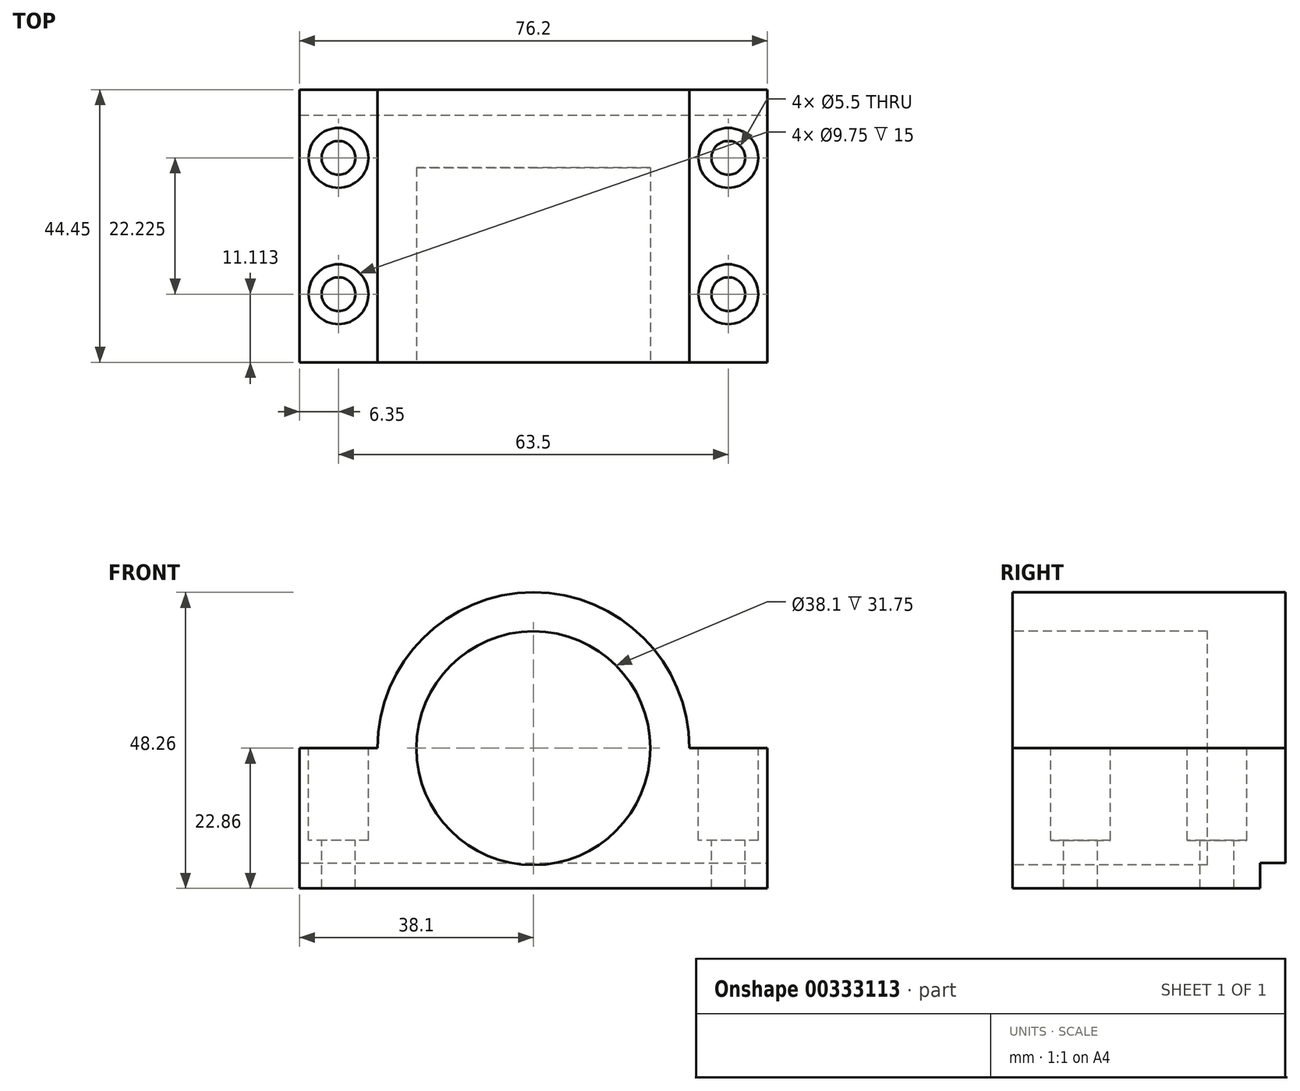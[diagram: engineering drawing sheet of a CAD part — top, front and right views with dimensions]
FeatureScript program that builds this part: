
annotation { "Feature Type Name" : "Feature", "Feature Type Description" : "" }
export const myFeature = defineFeature(function(context is Context, id is Id, definition is map)
    precondition{}
    {
        {
            var Q0;
            Q0=qCreatedBy(makeId("Front.planeOp"),FACE);
            var sketch = newSketch(context, id + "F0", { "sketchPlane" : qUnion([Q0])});
            skLineSegment(sketch, "E0.bottom", {"start": v(-38.1, -25.4) * mm, "end": v(38.1, -25.4) * mm});
            skLineSegment(sketch, "E0.top", {"start": v(-38.1, 25.4) * mm, "end": v(38.1, 25.4) * mm});
            skLineSegment(sketch, "E0.left", {"start": v(-38.1, -25.4) * mm, "end": v(-38.1, 25.4) * mm});
            skLineSegment(sketch, "E0.right", {"start": v(38.1, -25.4) * mm, "end": v(38.1, 25.4) * mm});
            skPoint(sketch, "E0.middle", {"position": v(0, 0) * mm});
            skSolve(sketch);
        }
        {
            var Q0;
            Q0=qSketchRegion(id+"F0",true);
            extrude(context, id + "F1", {"entities" : qUnion([Q0]), "depth" : 44.45 * mm});
        }
        {
            var Q0;
            Q0=makeQuery(id+"F1.opExtrude","CAP_FACE",FACE,{"disambiguationData":[OSD([sQuery(id+"F0.wireOp",EDGE,"E0.bottom"),sQuery(id+"F0.wireOp",EDGE,"E0.top"),sQuery(id+"F0.wireOp",EDGE,"E0.left"),sQuery(id+"F0.wireOp",EDGE,"E0.right")])],"isStart":false});
            var sketch = newSketch(context, id + "F2", { "sketchPlane" : qUnion([Q0])});
            skCircle(sketch, "E1", {"center": v(0, 0) * mm, "radius": 19.05 * mm});
            skSolve(sketch);
        }
        {
            var Q0;
            Q0=qSketchRegion(id+"F2",true);
            extrude(context, id + "F3", {"entities" : qUnion([Q0]), "operationType" : NewBodyOperationType.REMOVE, "oppositeDirection" : true, "depth" : 31.75 * mm});
        }
        {
            var Q0;
            Q0=makeQuery(id+"F1.opExtrude","CAP_FACE",FACE,{"disambiguationData":[OSD([sQuery(id+"F0.wireOp",EDGE,"E0.bottom"),sQuery(id+"F0.wireOp",EDGE,"E0.top"),sQuery(id+"F0.wireOp",EDGE,"E0.left"),sQuery(id+"F0.wireOp",EDGE,"E0.right")])],"isStart":false});
            var sketch = newSketch(context, id + "F4", { "sketchPlane" : qUnion([Q0])});
            skCircle(sketch, "E2.0", {"center": v(0, 0) * mm, "radius": 19.05 * mm});
            skCircle(sketch, "E3", {"center": v(0, 0) * mm, "radius": 25.4 * mm});
            skLineSegment(sketch, "E4", {"start": v(-38.1, 0) * mm, "end": v(-25.4, 0) * mm});
            skLineSegment(sketch, "E5", {"start": v(0, 0) * mm, "end": v(0, 26.24) * mm, "construction": true});
            skPoint(sketch, "E5.endSnap0", {"position": v(0, 25.4) * mm});
            skLineSegment(sketch, "E6.MirrorCS", {"start": v(38.1, 0) * mm, "end": v(25.4, 0) * mm});
            skSolve(sketch);
        }
        {
            var Q0;
            {var subQ0=sQuery(id+"F4.wireOp",EDGE,"E6.MirrorCS");Q0=makeQuery(id+"F4.imprint","IMPRINT",FACE,{"disambiguationData":[TD([[makeQuery(id+"F4.imprint","IMPRINT",EDGE,{"derivedFrom":subQ0}),-1.0]])]});}
            var Q1;
            {var subQ0=sQuery(id+"F4.wireOp",EDGE,"E4");Q1=makeQuery(id+"F4.imprint","IMPRINT",FACE,{"disambiguationData":[TD([[makeQuery(id+"F4.imprint","IMPRINT",EDGE,{"derivedFrom":subQ0}),1.0]])]});}
            extrude(context, id + "F5", {"entities" : qUnion([Q0, Q1]), "operationType" : NewBodyOperationType.REMOVE, "oppositeDirection" : true, "depth" : 63 * mm});
        }
        {
            var Q0;
            Q0=makeQuery(id+"F5.boolean.opBoolean","COPY",FACE,{"derivedFrom":makeQuery(id+"F5.opExtrude","SWEPT_FACE",FACE,{"disambiguationData":[OSD([sQuery(id+"F4.wireOp",EDGE,"E4")])]})});
            var sketch = newSketch(context, id + "F6", { "sketchPlane" : qUnion([Q0])});
            skPoint(sketch, "E7", {"position": v(-31.75, -11.11) * mm});
            skPoint(sketch, "E8", {"position": v(-31.75, -33.34) * mm});
            skPoint(sketch, "E9", {"position": v(31.75, -11.11) * mm});
            skPoint(sketch, "E10", {"position": v(31.75, -33.34) * mm});
            skLineSegment(sketch, "E11", {"start": v(0, 0) * mm, "end": v(0, -44.43) * mm, "construction": true});
            skLineSegment(sketch, "E12.0", {"start": v(25.4, 0) * mm, "end": v(25.4, -44.45) * mm});
            skLineSegment(sketch, "E13.0", {"start": v(38.1, 0) * mm, "end": v(38.1, -44.45) * mm});
            skLineSegment(sketch, "E14", {"start": v(31.75, -44.45) * mm, "end": v(31.75, -41.85) * mm, "construction": true});
            skLineSegment(sketch, "E15.0", {"start": v(38.1, -44.45) * mm, "end": v(25.4, -44.45) * mm});
            skLineSegment(sketch, "E16", {"start": v(-38.1, -22.23) * mm, "end": v(38.1, -22.23) * mm, "construction": true});
            skLineSegment(sketch, "E17", {"start": v(-38.1, -22.23) * mm, "end": v(-38.1, 0) * mm, "construction": true});
            skLineSegment(sketch, "E18", {"start": v(-38.1, 0) * mm, "end": v(-38.1, -11.11) * mm, "construction": true});
            skLineSegment(sketch, "E19", {"start": v(-38.1, -11.11) * mm, "end": v(-35.36, -11.11) * mm, "construction": true});
            skSolve(sketch);
        }
        {
            var Q0;
            Q0=sQuery(id+"F6.wireOp",VERTEX,"E7");
            var Q1;
            Q1=sQuery(id+"F6.wireOp",VERTEX,"E8");
            var Q2;
            Q2=sQuery(id+"F6.wireOp",VERTEX,"E10");
            var Q3;
            Q3=sQuery(id+"F6.wireOp",VERTEX,"E9");
            var Q4;
            Q4=makeQuery(id+"F1.opExtrude","SWEPT_BODY",BODY,{"disambiguationData":[OSD([sQuery(id+"F0.wireOp",EDGE,"E0.bottom"),sQuery(id+"F0.wireOp",EDGE,"E0.top"),sQuery(id+"F0.wireOp",EDGE,"E0.left"),sQuery(id+"F0.wireOp",EDGE,"E0.right")])]});
            hole(context, id + "F7", {"style" : HoleStyle.C_BORE, "endStyle" : HoleEndStyle.BLIND, "holeDiameter" : 5.5 * mm, "cBoreDiameter" : 9.75 * mm, "cBoreDepth" : 15 * mm, "holeDepth" : 254 * mm, "tappedDepth" : 12.7 * mm, "tapClearance" : 3, "locations" : qUnion([Q0, Q1, Q2, Q3]), "scope" : qUnion([Q4])});
        }
        {
            var Q0;
            Q0=makeQuery(id+"F1.opExtrude","SWEPT_FACE",FACE,{"disambiguationData":[OSD([sQuery(id+"F0.wireOp",EDGE,"E0.bottom")])]});
            extrude(context, id + "F8", {"entities" : qUnion([Q0]), "operationType" : NewBodyOperationType.REMOVE, "oppositeDirection" : true, "depth" : 2.54 * mm});
        }
        {
            var Q0;
            Q0=makeQuery(id+"F1.opExtrude","SWEPT_FACE",FACE,{"disambiguationData":[OSD([sQuery(id+"F0.wireOp",EDGE,"E0.right")])]});
            var sketch = newSketch(context, id + "F9", { "sketchPlane" : qUnion([Q0])});
            skLineSegment(sketch, "E20.bottom", {"start": v(0, -22.86) * mm, "end": v(-4.13, -22.86) * mm});
            skLineSegment(sketch, "E20.top", {"start": v(0, -18.73) * mm, "end": v(-4.13, -18.73) * mm});
            skLineSegment(sketch, "E20.left", {"start": v(0, -22.86) * mm, "end": v(0, -18.73) * mm});
            skLineSegment(sketch, "E20.right", {"start": v(-4.13, -22.86) * mm, "end": v(-4.13, -18.73) * mm});
            skSolve(sketch);
        }
        {
            var Q0;
            Q0=qSketchRegion(id+"F9",true);
            extrude(context, id + "F10", {"entities" : qUnion([Q0]), "operationType" : NewBodyOperationType.REMOVE, "oppositeDirection" : true, "depth" : 86.36 * mm});
        }
    });
